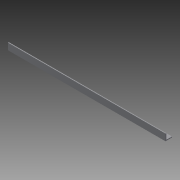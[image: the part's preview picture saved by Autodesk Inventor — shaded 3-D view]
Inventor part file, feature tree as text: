
AUTODESK INVENTOR PART (.ipt)
format: ipt  version: 2015 (Build 190159000, 159)  size: 91,136 bytes
history: native  units: in
note: dims shown in document units (in); Inventor stores cm internally (conversion verified against a paired STEP export)
features: sketch x2, extrude x1, hole x1, projected_geometry x1
ambient origin geometry x8: Origin, YZ Plane, XZ Plane, XY Plane, X Axis, Y Axis, Z Axis, Center Point
bodies: Solid1 (feature_tree)
feature tree (5):
  extrude  "Extrusion1"  Depth=0.125in
  hole  "Hole1"  [1 undecoded]
  sketch  "Sketch1"  dims[d0=1.0in d1=0.125in]
  sketch  "Sketch2"  dims[d2=0.125in d3=1.0in d4=23.75in d5=0.0in d6=0.5in d7=0.5in d8=0.5in d9=0.5in d10=0.5in d11=0.5in d12=10.875in d13=10.875in d14=0.25in d15=0.75in d16=0.375in d17=0.25in d18=0.5635in d19=1.0in d20=0.8108in]
  projected_geometry  "Projected Loop1"
note: 1 required parameter value undecoded (feature->parameter linkage not recoverable at this tier; creation-order binding heuristic only, values carry confidence <= 0.55)
